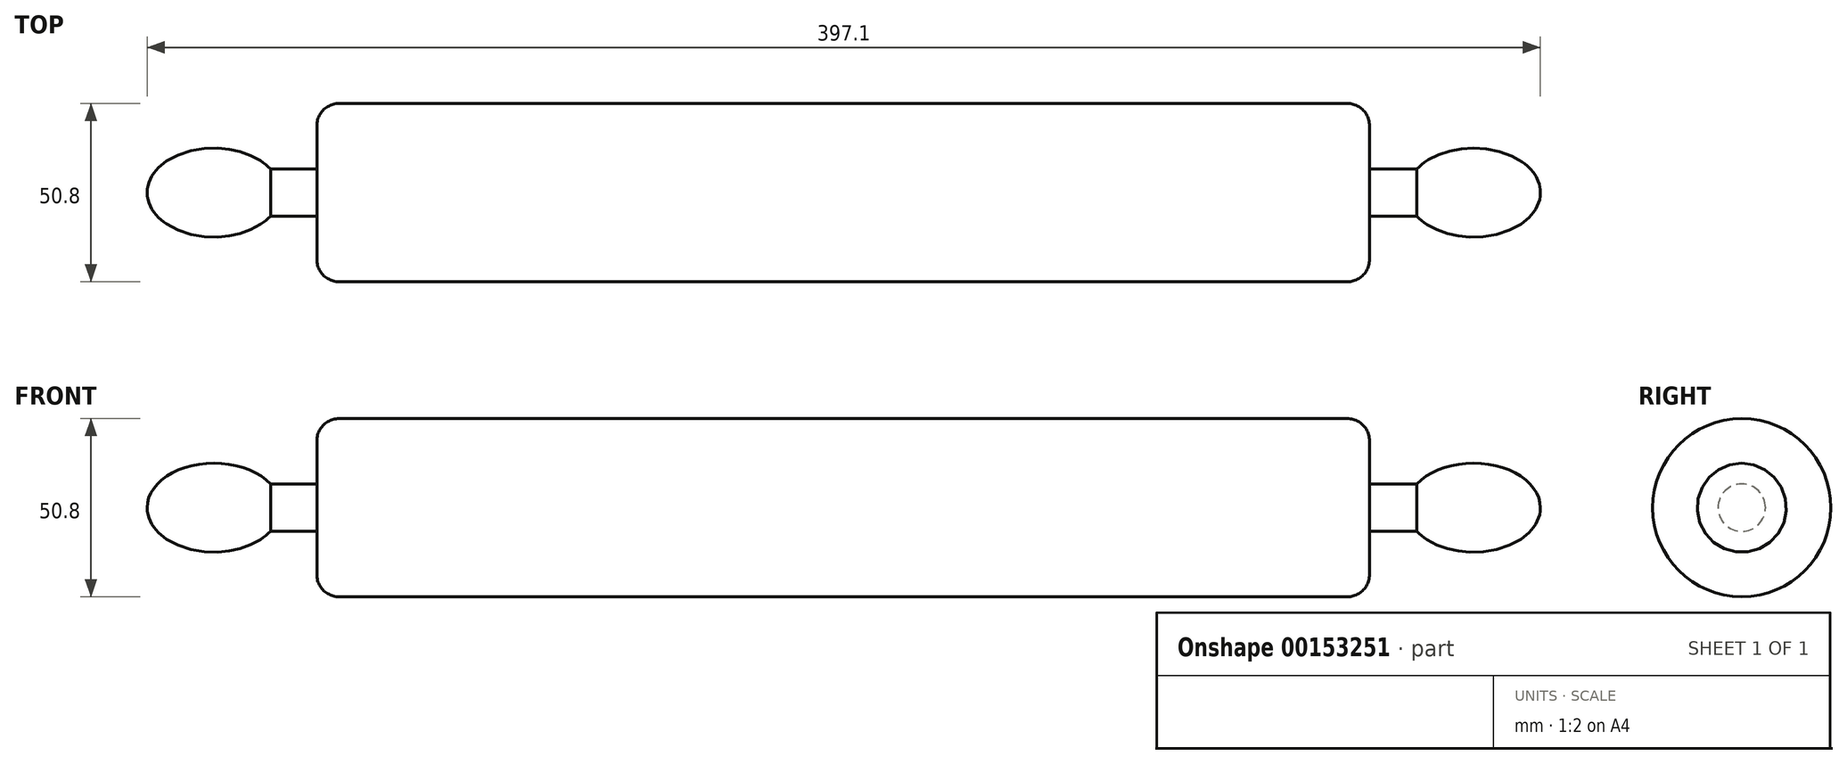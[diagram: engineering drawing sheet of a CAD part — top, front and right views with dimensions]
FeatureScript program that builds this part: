
annotation { "Feature Type Name" : "Feature", "Feature Type Description" : "" }
export const myFeature = defineFeature(function(context is Context, id is Id, definition is map)
    precondition{}
    {
        {
            var Q0;
            Q0=qCreatedBy(makeId("Front.planeOp"),FACE);
            var sketch = newSketch(context, id + "F0", { "sketchPlane" : qUnion([Q0])});
            skLineSegment(sketch, "E0.top", {"start": v(-109.59, 25.4) * mm, "end": v(177.71, 25.4) * mm});
            skLineSegment(sketch, "E0.left", {"start": v(-115.94, 6.75) * mm, "end": v(-115.94, 19.05) * mm});
            skLineSegment(sketch, "E0.right", {"start": v(184.06, 6.75) * mm, "end": v(184.06, 19.05) * mm});
            skEllipticalArc(sketch, "E1", {});
            skEllipticalArc(sketch, "E2", {});
            skPoint(sketch, "E3.visualSharp", {"position": v(-115.94, 25.4) * mm});
            skArc(sketch, "E3.filletArc", {"start": v(-109.59, 25.4) * mm, "mid": v(-114.08, 23.54) * mm, "end": v(-115.94, 19.05) * mm});
            skPoint(sketch, "E4.visualSharp", {"position": v(184.06, 25.4) * mm});
            skArc(sketch, "E4.filletArc", {"start": v(184.06, 19.05) * mm, "mid": v(182.2, 23.54) * mm, "end": v(177.71, 25.4) * mm});
            skLineSegment(sketch, "E5", {"start": v(-129.16, 6.75) * mm, "end": v(-115.94, 6.75) * mm});
            skLineSegment(sketch, "E6", {"start": v(184.06, 6.75) * mm, "end": v(197.6, 6.75) * mm});
            skLineSegment(sketch, "E7", {"start": v(-164.32, 0) * mm, "end": v(232.78, 0) * mm});
            const initialGuessF0  = {"E1": [-0.14527878165245056, 0, -1, 0, 0.01903682215055269, 0.012691214767035127, 3.7022890268073447, 0], "E2": [0.2137279510498047, 0, -1, 0, 0.01905, 0.0127, 3.141592653589793, 5.7229232388465]};
            skSetInitialGuess(sketch, initialGuessF0);
            skSolve(sketch);
        }
        {
            var Q0;
            Q0=makeQuery(id+"F0.imprint","IMPRINT",FACE,{"disambiguationData":[TD([[makeQuery(id+"F0.imprint","IMPRINT",EDGE,{"derivedFrom":sQuery(id+"F0.wireOp",EDGE,"E0.top")}),-1.0]])]});
            var Q1;
            Q1=sQuery(id+"F0.wireOp",EDGE,"E7");
            revolve(context, id + "F1", {"entities" : qUnion([Q0]), "axis" : qUnion([Q1]), "revolveType" : RevolveType.FULL});
        }
    });
